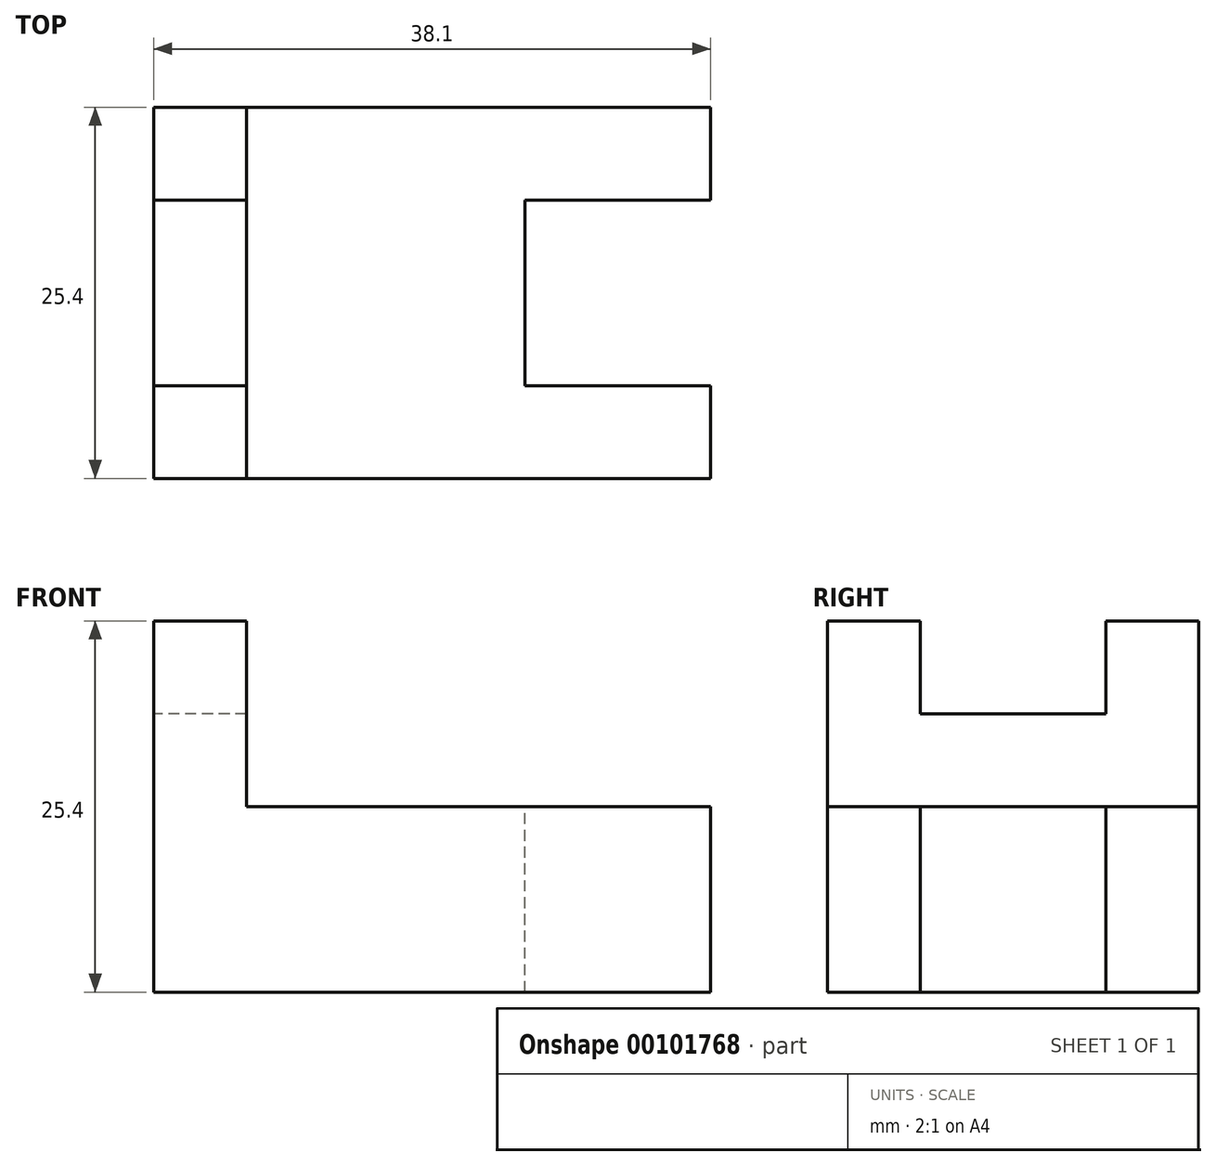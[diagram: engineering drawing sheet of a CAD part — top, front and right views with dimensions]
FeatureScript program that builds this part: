
annotation { "Feature Type Name" : "Feature", "Feature Type Description" : "" }
export const myFeature = defineFeature(function(context is Context, id is Id, definition is map)
    precondition{}
    {
        {
            var Q0;
            Q0=qCreatedBy(makeId("Front.planeOp"),FACE);
            var sketch = newSketch(context, id + "F0", { "sketchPlane" : qUnion([Q0])});
            skLineSegment(sketch, "E0", {"start": v(0, 0) * mm, "end": v(0, 25.4) * mm});
            skLineSegment(sketch, "E1", {"start": v(0, 25.4) * mm, "end": v(6.35, 25.4) * mm});
            skLineSegment(sketch, "E2", {"start": v(6.35, 25.4) * mm, "end": v(6.35, 12.7) * mm});
            skLineSegment(sketch, "E3", {"start": v(6.35, 12.7) * mm, "end": v(38.1, 12.7) * mm});
            skLineSegment(sketch, "E4", {"start": v(38.1, 12.7) * mm, "end": v(38.1, 0) * mm});
            skLineSegment(sketch, "E5", {"start": v(38.1, 0) * mm, "end": v(0, 0) * mm});
            skSolve(sketch);
        }
        {
            var Q0;
            Q0 = qSketchRegion(id + "F0", true);
            extrude(context, id + "F1", {"entities" : qUnion([Q0]), "endBound" : BoundingType.SYMMETRIC, "depth" : 25.4 * mm});
        }
        {
            var Q0;
            Q0=qCreatedBy(makeId("Front.planeOp"),FACE);
            var sketch = newSketch(context, id + "F2", { "sketchPlane" : qUnion([Q0])});
            skLineSegment(sketch, "E6", {"start": v(38.1, 12.7) * mm, "end": v(38.1, 0) * mm});
            skLineSegment(sketch, "E7", {"start": v(38.1, 0) * mm, "end": v(25.4, 0) * mm});
            skLineSegment(sketch, "E8", {"start": v(25.4, 0) * mm, "end": v(25.4, 12.7) * mm});
            skLineSegment(sketch, "E9", {"start": v(25.4, 12.7) * mm, "end": v(38.1, 12.7) * mm});
            skSolve(sketch);
        }
        {
            var Q0;
            Q0 = qSketchRegion(id + "F2", true);
            extrude(context, id + "F3", {"entities" : qUnion([Q0]), "operationType" : NewBodyOperationType.REMOVE, "endBound" : BoundingType.SYMMETRIC, "oppositeDirection" : true, "depth" : 12.7 * mm});
        }
        {
            var Q0;
            Q0=qCreatedBy(makeId("Front.planeOp"),FACE);
            var sketch = newSketch(context, id + "F4", { "sketchPlane" : qUnion([Q0])});
            skLineSegment(sketch, "E10", {"start": v(0, 25.4) * mm, "end": v(6.35, 25.4) * mm});
            skLineSegment(sketch, "E11", {"start": v(6.35, 25.4) * mm, "end": v(6.35, 19.05) * mm});
            skLineSegment(sketch, "E12", {"start": v(6.35, 19.05) * mm, "end": v(0, 19.05) * mm});
            skLineSegment(sketch, "E13", {"start": v(0, 19.05) * mm, "end": v(0, 25.4) * mm});
            skSolve(sketch);
        }
        {
            var Q0;
            Q0 = qSketchRegion(id + "F4", true);
            extrude(context, id + "F5", {"entities" : qUnion([Q0]), "operationType" : NewBodyOperationType.REMOVE, "endBound" : BoundingType.SYMMETRIC, "depth" : 12.7 * mm});
        }
    });
